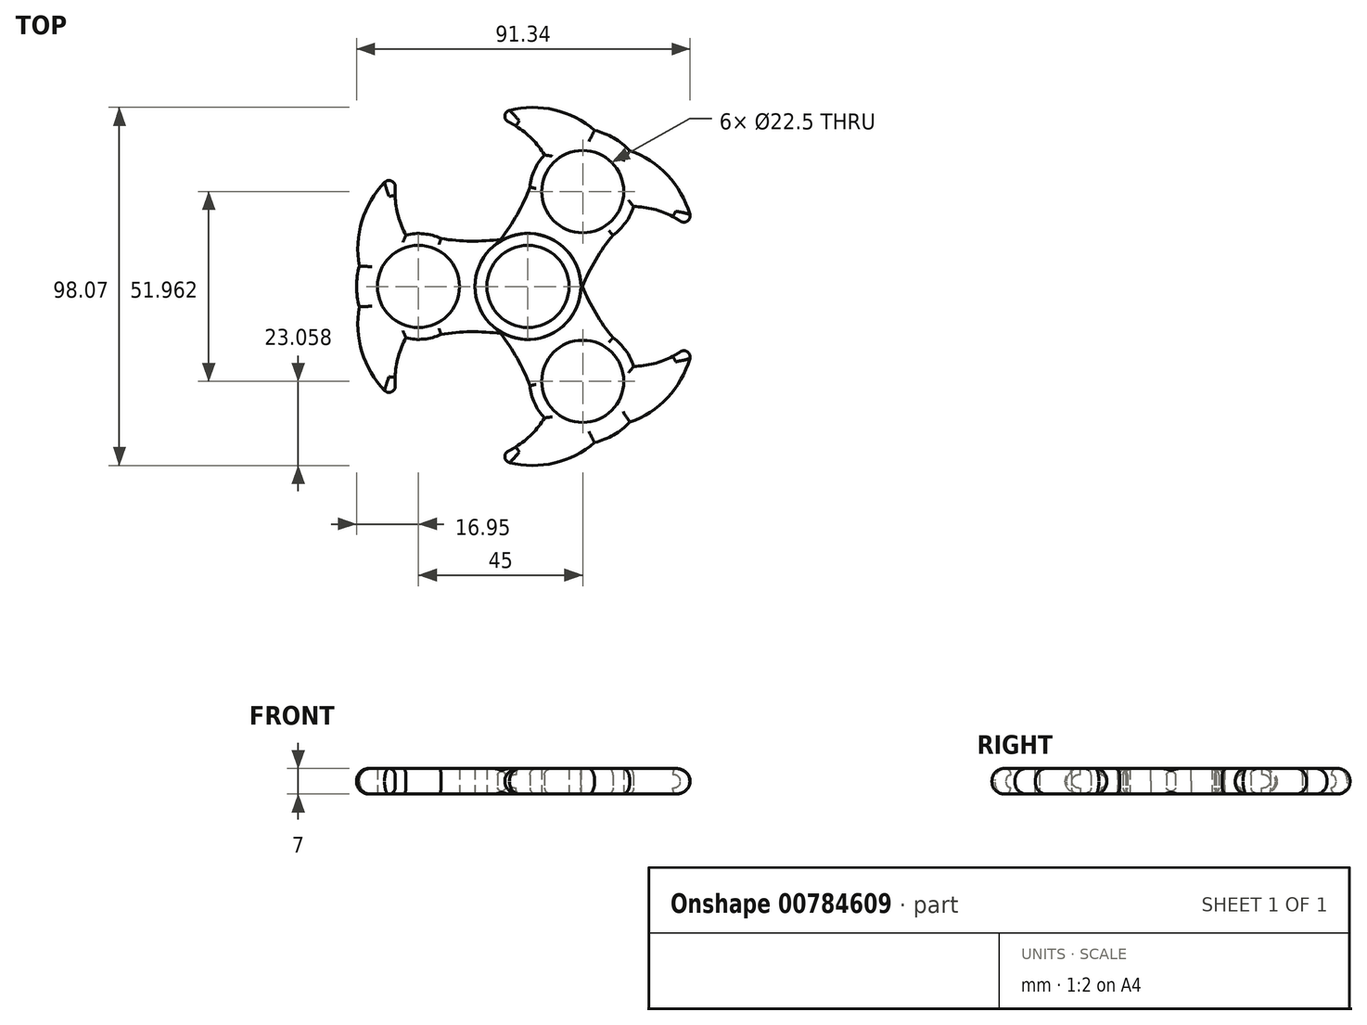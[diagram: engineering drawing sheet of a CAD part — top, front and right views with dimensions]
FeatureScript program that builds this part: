
annotation { "Feature Type Name" : "Feature", "Feature Type Description" : "" }
export const myFeature = defineFeature(function(context is Context, id is Id, definition is map)
    precondition{}
    {
        {
            var Q0;
            Q0=qCreatedBy(makeId("Top.planeOp"),FACE);
            var sketch = newSketch(context, id + "F0", { "sketchPlane" : qUnion([Q0])});
            skCircle(sketch, "E0", {"center": v(0, 0) * mm, "radius": 11.25 * mm});
            skLineSegment(sketch, "E1", {"start": v(0, 0) * mm, "end": v(-30, 0) * mm});
            skCircle(sketch, "E2", {"center": v(-30, 0) * mm, "radius": 11.25 * mm});
            skCircle(sketch, "E3", {"center": v(-30, 0) * mm, "radius": 14.5 * mm});
            skCircle(sketch, "E4", {"center": v(0, 0) * mm, "radius": 14.5 * mm});
            skArc(sketch, "E5", {"start": v(0, -14.5) * mm, "mid": v(-15, -12.4) * mm, "end": v(-30, -14.5) * mm});
            skArc(sketch, "E6.MirrorCS", {"start": v(0, 14.5) * mm, "mid": v(-15, 12.41) * mm, "end": v(-30, 14.5) * mm});
            skArc(sketch, "E7", {"start": v(-33.43, -14.08) * mm, "mid": v(-36.22, -22.63) * mm, "end": v(-35.67, -31.61) * mm});
            skArc(sketch, "E8", {"start": v(-44.5, 0) * mm, "mid": v(-45.64, -17.36) * mm, "end": v(-35.67, -31.61) * mm});
            skArc(sketch, "E9.MirrorCS", {"start": v(-33.43, 14.1) * mm, "mid": v(-36.22, 22.65) * mm, "end": v(-35.67, 31.63) * mm});
            skArc(sketch, "E10.MirrorCS", {"start": v(-44.5, 0.02) * mm, "mid": v(-45.64, 17.38) * mm, "end": v(-35.67, 31.63) * mm});
            skLineSegment(sketch, "E11", {"start": v(-44.5, 0.02) * mm, "end": v(-46.18, 0.02) * mm});
            skArc(sketch, "E12", {"start": v(-46.18, 5.59) * mm, "mid": v(-46.95, 0) * mm, "end": v(-46.18, -5.57) * mm});
            skSolve(sketch);
        }
        {
            var Q0;
            Q0 = qSketchRegion(id + "F0", true);
            extrude(context, id + "F1", {"entities" : qUnion([Q0]), "depth" : 7 * mm, "offsetDistance" : 25 * mm});
        }
        {
            var Q0;
            Q0=makeQuery(id+"F1.opExtrude","SWEPT_BODY",BODY,{"disambiguationData":[OSD([sQuery(id+"F0.wireOp",EDGE,"E0"),sQuery(id+"F0.wireOp",EDGE,"E2"),sQuery(id+"F0.wireOp",EDGE,"E3"),sQuery(id+"F0.wireOp",EDGE,"E4"),sQuery(id+"F0.wireOp",EDGE,"E5"),sQuery(id+"F0.wireOp",EDGE,"E6.MirrorCS"),sQuery(id+"F0.wireOp",EDGE,"N5z0aknD-i1vi-YF0C-1aPX-2y42hYEXv3Ia"),sQuery(id+"F0.wireOp",EDGE,"vDmnVq8P-OYbs-Mt9C-JsBL-gKGyEo7dJEWc")])]});
            var Q1;
            Q1=makeQuery(id+"F1.opExtrude","SWEPT_FACE",FACE,{"disambiguationData":[OSD([sQuery(id+"F0.wireOp",EDGE,"E4")])]});
            circularPattern(context, id + "F2", {"entities" : qUnion([Q0]), "axis" : qUnion([Q1]), "angle" : 360 * degree, "instanceCount" : 3, "equalSpace" : true});
        }
        {
            var Q0;
            Q0=makeQuery(id+"F2.opPattern","COPY",EDGE,{"derivedFrom":makeQuery(id+"F1.opExtrude","CAP_EDGE",EDGE,{"disambiguationData":[OSD([sQuery(id+"F0.wireOp",EDGE,"E10.MirrorCS")])],"isStart":false}),"instanceName":"2"});
            var Q1;
            Q1=makeQuery(id+"F2.opPattern","COPY",EDGE,{"derivedFrom":makeQuery(id+"F1.opExtrude","CAP_EDGE",EDGE,{"disambiguationData":[OSD([sQuery(id+"F0.wireOp",EDGE,"E12")])],"isStart":false}),"instanceName":"2"});
            var Q2;
            Q2=makeQuery(id+"F2.opPattern","COPY",EDGE,{"derivedFrom":makeQuery(id+"F1.opExtrude","CAP_EDGE",EDGE,{"disambiguationData":[OSD([sQuery(id+"F0.wireOp",EDGE,"E8")])],"isStart":false}),"instanceName":"2"});
            var Q3;
            Q3=makeQuery(id+"F2.opPattern","COPY",EDGE,{"derivedFrom":makeQuery(id+"F1.opExtrude","CAP_EDGE",EDGE,{"disambiguationData":[OSD([sQuery(id+"F0.wireOp",EDGE,"E10.MirrorCS")])],"isStart":false}),"instanceName":"1"});
            var Q4;
            Q4=makeQuery(id+"F2.opPattern","COPY",EDGE,{"derivedFrom":makeQuery(id+"F1.opExtrude","CAP_EDGE",EDGE,{"disambiguationData":[OSD([sQuery(id+"F0.wireOp",EDGE,"E12")])],"isStart":false}),"instanceName":"1"});
            var Q5;
            Q5=makeQuery(id+"F2.opPattern","COPY",EDGE,{"derivedFrom":makeQuery(id+"F1.opExtrude","CAP_EDGE",EDGE,{"disambiguationData":[OSD([sQuery(id+"F0.wireOp",EDGE,"E8")])],"isStart":false}),"instanceName":"1"});
            var Q6;
            Q6=makeQuery(id+"F1.opExtrude","CAP_EDGE",EDGE,{"disambiguationData":[OSD([sQuery(id+"F0.wireOp",EDGE,"E10.MirrorCS")])],"isStart":false});
            var Q7;
            Q7=makeQuery(id+"F1.opExtrude","CAP_EDGE",EDGE,{"disambiguationData":[OSD([sQuery(id+"F0.wireOp",EDGE,"E12")])],"isStart":false});
            var Q8;
            Q8=makeQuery(id+"F1.opExtrude","CAP_EDGE",EDGE,{"disambiguationData":[OSD([sQuery(id+"F0.wireOp",EDGE,"E8")])],"isStart":false});
            var Q9;
            Q9=makeQuery(id+"F1.opExtrude","CAP_EDGE",EDGE,{"disambiguationData":[OSD([sQuery(id+"F0.wireOp",EDGE,"E12")])],"isStart":true});
            var Q10;
            Q10=makeQuery(id+"F1.opExtrude","CAP_EDGE",EDGE,{"disambiguationData":[OSD([sQuery(id+"F0.wireOp",EDGE,"E8")])],"isStart":true});
            var Q11;
            Q11=makeQuery(id+"F1.opExtrude","CAP_EDGE",EDGE,{"disambiguationData":[OSD([sQuery(id+"F0.wireOp",EDGE,"E10.MirrorCS")])],"isStart":true});
            var Q12;
            Q12=makeQuery(id+"F2.opPattern","COPY",EDGE,{"derivedFrom":makeQuery(id+"F1.opExtrude","CAP_EDGE",EDGE,{"disambiguationData":[OSD([sQuery(id+"F0.wireOp",EDGE,"E12")])],"isStart":true}),"instanceName":"2"});
            var Q13;
            Q13=makeQuery(id+"F2.opPattern","COPY",EDGE,{"derivedFrom":makeQuery(id+"F1.opExtrude","CAP_EDGE",EDGE,{"disambiguationData":[OSD([sQuery(id+"F0.wireOp",EDGE,"E8")])],"isStart":true}),"instanceName":"2"});
            var Q14;
            Q14=makeQuery(id+"F2.opPattern","COPY",EDGE,{"derivedFrom":makeQuery(id+"F1.opExtrude","CAP_EDGE",EDGE,{"disambiguationData":[OSD([sQuery(id+"F0.wireOp",EDGE,"E10.MirrorCS")])],"isStart":true}),"instanceName":"2"});
            var Q15;
            Q15=makeQuery(id+"F2.opPattern","COPY",EDGE,{"derivedFrom":makeQuery(id+"F1.opExtrude","CAP_EDGE",EDGE,{"disambiguationData":[OSD([sQuery(id+"F0.wireOp",EDGE,"E10.MirrorCS")])],"isStart":true}),"instanceName":"1"});
            var Q16;
            Q16=makeQuery(id+"F2.opPattern","COPY",EDGE,{"derivedFrom":makeQuery(id+"F1.opExtrude","CAP_EDGE",EDGE,{"disambiguationData":[OSD([sQuery(id+"F0.wireOp",EDGE,"E12")])],"isStart":true}),"instanceName":"1"});
            var Q17;
            Q17=makeQuery(id+"F2.opPattern","COPY",EDGE,{"derivedFrom":makeQuery(id+"F1.opExtrude","CAP_EDGE",EDGE,{"disambiguationData":[OSD([sQuery(id+"F0.wireOp",EDGE,"E8")])],"isStart":true}),"instanceName":"1"});
            fillet(context, id + "F3", {"entities" : qUnion([Q0, Q1, Q2, Q3, Q4, Q5, Q6, Q7, Q8, Q9, Q10, Q11, Q12, Q13, Q14, Q15, Q16, Q17]), "radius" : 3.38 * mm, "tangentPropagation" : true, "allowEdgeOverflow" : false});
        }
        {
            var Q0;
            Q0=makeQuery(id+"F2.opPattern","COPY",EDGE,{"derivedFrom":makeQuery(id+"F1.opExtrude","CAP_EDGE",EDGE,{"disambiguationData":[OSD([sQuery(id+"F0.wireOp",EDGE,"E6.MirrorCS")])],"isStart":true}),"instanceName":"2"});
            var Q1;
            Q1=makeQuery(id+"F1.opExtrude","CAP_EDGE",EDGE,{"disambiguationData":[OSD([sQuery(id+"F0.wireOp",EDGE,"E5")])],"isStart":true});
            var Q2;
            Q2=makeQuery(id+"F2.opPattern","COPY",EDGE,{"derivedFrom":makeQuery(id+"F1.opExtrude","CAP_EDGE",EDGE,{"disambiguationData":[OSD([sQuery(id+"F0.wireOp",EDGE,"E5")])],"isStart":true}),"instanceName":"2"});
            var Q3;
            Q3=makeQuery(id+"F2.opPattern","COPY",EDGE,{"derivedFrom":makeQuery(id+"F1.opExtrude","CAP_EDGE",EDGE,{"disambiguationData":[OSD([sQuery(id+"F0.wireOp",EDGE,"E6.MirrorCS")])],"isStart":true}),"instanceName":"1"});
            var Q4;
            Q4=makeQuery(id+"F2.opPattern","COPY",EDGE,{"derivedFrom":makeQuery(id+"F1.opExtrude","CAP_EDGE",EDGE,{"disambiguationData":[OSD([sQuery(id+"F0.wireOp",EDGE,"E5")])],"isStart":true}),"instanceName":"1"});
            var Q5;
            Q5=makeQuery(id+"F1.opExtrude","CAP_EDGE",EDGE,{"disambiguationData":[OSD([sQuery(id+"F0.wireOp",EDGE,"E6.MirrorCS")])],"isStart":true});
            var Q6;
            {var subQ0=sQuery(id+"F0.wireOp",EDGE,"E6.MirrorCS");var subQ1=sQuery(id+"F0.wireOp",EDGE,"E3");var subQ2=makeQuery(id+"F0.imprint","INTERSECT",VERTEX,{"disambiguationData":[OD(0.0)],"derivedFrom":[subQ1,subQ0]});Q6=makeQuery(id+"F1.opExtrude","CAP_EDGE",EDGE,{"disambiguationData":[OSD([subQ1]),TDD([makeQuery(id+"F0.imprint","IMPRINT",EDGE,{"disambiguationData":[TD([[subQ2,1.0]])],"derivedFrom":subQ1}),makeQuery(id+"F0.imprint","IMPRINT",EDGE,{"disambiguationData":[TD([[subQ2,-1.0]])],"derivedFrom":subQ1})])],"isStart":true});}
            var Q7;
            {var subQ0=sQuery(id+"F0.wireOp",EDGE,"E5");var subQ1=sQuery(id+"F0.wireOp",EDGE,"E3");var subQ2=makeQuery(id+"F0.imprint","INTERSECT",VERTEX,{"disambiguationData":[OD(0.0)],"derivedFrom":[subQ1,subQ0]});Q7=makeQuery(id+"F2.opPattern","COPY",EDGE,{"derivedFrom":makeQuery(id+"F1.opExtrude","CAP_EDGE",EDGE,{"disambiguationData":[OSD([subQ1]),TDD([makeQuery(id+"F0.imprint","IMPRINT",EDGE,{"disambiguationData":[TD([[subQ2,1.0]])],"derivedFrom":subQ1}),makeQuery(id+"F0.imprint","IMPRINT",EDGE,{"disambiguationData":[TD([[subQ2,-1.0]])],"derivedFrom":subQ1})])],"isStart":true}),"instanceName":"1"});}
            var Q8;
            {var subQ0=sQuery(id+"F0.wireOp",EDGE,"E6.MirrorCS");var subQ1=sQuery(id+"F0.wireOp",EDGE,"E3");var subQ2=makeQuery(id+"F0.imprint","INTERSECT",VERTEX,{"disambiguationData":[OD(0.0)],"derivedFrom":[subQ1,subQ0]});Q8=makeQuery(id+"F2.opPattern","COPY",EDGE,{"derivedFrom":makeQuery(id+"F1.opExtrude","CAP_EDGE",EDGE,{"disambiguationData":[OSD([subQ1]),TDD([makeQuery(id+"F0.imprint","IMPRINT",EDGE,{"disambiguationData":[TD([[subQ2,1.0]])],"derivedFrom":subQ1}),makeQuery(id+"F0.imprint","IMPRINT",EDGE,{"disambiguationData":[TD([[subQ2,-1.0]])],"derivedFrom":subQ1})])],"isStart":true}),"instanceName":"1"});}
            var Q9;
            {var subQ0=sQuery(id+"F0.wireOp",EDGE,"E6.MirrorCS");var subQ1=sQuery(id+"F0.wireOp",EDGE,"E3");var subQ2=makeQuery(id+"F0.imprint","INTERSECT",VERTEX,{"disambiguationData":[OD(0.0)],"derivedFrom":[subQ1,subQ0]});Q9=makeQuery(id+"F2.opPattern","COPY",EDGE,{"derivedFrom":makeQuery(id+"F1.opExtrude","CAP_EDGE",EDGE,{"disambiguationData":[OSD([subQ1]),TDD([makeQuery(id+"F0.imprint","IMPRINT",EDGE,{"disambiguationData":[TD([[subQ2,1.0]])],"derivedFrom":subQ1}),makeQuery(id+"F0.imprint","IMPRINT",EDGE,{"disambiguationData":[TD([[subQ2,-1.0]])],"derivedFrom":subQ1})])],"isStart":true}),"instanceName":"2"});}
            var Q10;
            {var subQ0=sQuery(id+"F0.wireOp",EDGE,"E5");var subQ1=sQuery(id+"F0.wireOp",EDGE,"E3");var subQ2=makeQuery(id+"F0.imprint","INTERSECT",VERTEX,{"disambiguationData":[OD(0.0)],"derivedFrom":[subQ1,subQ0]});Q10=makeQuery(id+"F1.opExtrude","CAP_EDGE",EDGE,{"disambiguationData":[OSD([subQ1]),TDD([makeQuery(id+"F0.imprint","IMPRINT",EDGE,{"disambiguationData":[TD([[subQ2,1.0]])],"derivedFrom":subQ1}),makeQuery(id+"F0.imprint","IMPRINT",EDGE,{"disambiguationData":[TD([[subQ2,-1.0]])],"derivedFrom":subQ1})])],"isStart":true});}
            var Q11;
            {var subQ0=sQuery(id+"F0.wireOp",EDGE,"E5");var subQ1=sQuery(id+"F0.wireOp",EDGE,"E3");var subQ2=makeQuery(id+"F0.imprint","INTERSECT",VERTEX,{"disambiguationData":[OD(0.0)],"derivedFrom":[subQ1,subQ0]});Q11=makeQuery(id+"F2.opPattern","COPY",EDGE,{"derivedFrom":makeQuery(id+"F1.opExtrude","CAP_EDGE",EDGE,{"disambiguationData":[OSD([subQ1]),TDD([makeQuery(id+"F0.imprint","IMPRINT",EDGE,{"disambiguationData":[TD([[subQ2,1.0]])],"derivedFrom":subQ1}),makeQuery(id+"F0.imprint","IMPRINT",EDGE,{"disambiguationData":[TD([[subQ2,-1.0]])],"derivedFrom":subQ1})])],"isStart":true}),"instanceName":"2"});}
            var Q12;
            {var subQ0=sQuery(id+"F0.wireOp",EDGE,"E6.MirrorCS");var subQ1=sQuery(id+"F0.wireOp",EDGE,"E3");var subQ2=makeQuery(id+"F0.imprint","INTERSECT",VERTEX,{"disambiguationData":[OD(0.0)],"derivedFrom":[subQ1,subQ0]});Q12=makeQuery(id+"F2.opPattern","COPY",EDGE,{"derivedFrom":makeQuery(id+"F1.opExtrude","CAP_EDGE",EDGE,{"disambiguationData":[OSD([subQ1]),TDD([makeQuery(id+"F0.imprint","IMPRINT",EDGE,{"disambiguationData":[TD([[subQ2,1.0]])],"derivedFrom":subQ1}),makeQuery(id+"F0.imprint","IMPRINT",EDGE,{"disambiguationData":[TD([[subQ2,-1.0]])],"derivedFrom":subQ1})])],"isStart":false}),"instanceName":"2"});}
            var Q13;
            Q13=makeQuery(id+"F2.opPattern","COPY",EDGE,{"derivedFrom":makeQuery(id+"F1.opExtrude","CAP_EDGE",EDGE,{"disambiguationData":[OSD([sQuery(id+"F0.wireOp",EDGE,"E6.MirrorCS")])],"isStart":false}),"instanceName":"2"});
            var Q14;
            Q14=makeQuery(id+"F1.opExtrude","CAP_EDGE",EDGE,{"disambiguationData":[OSD([sQuery(id+"F0.wireOp",EDGE,"E5")])],"isStart":false});
            var Q15;
            {var subQ0=sQuery(id+"F0.wireOp",EDGE,"E5");var subQ1=sQuery(id+"F0.wireOp",EDGE,"E3");var subQ2=makeQuery(id+"F0.imprint","INTERSECT",VERTEX,{"disambiguationData":[OD(0.0)],"derivedFrom":[subQ1,subQ0]});Q15=makeQuery(id+"F1.opExtrude","CAP_EDGE",EDGE,{"disambiguationData":[OSD([subQ1]),TDD([makeQuery(id+"F0.imprint","IMPRINT",EDGE,{"disambiguationData":[TD([[subQ2,1.0]])],"derivedFrom":subQ1}),makeQuery(id+"F0.imprint","IMPRINT",EDGE,{"disambiguationData":[TD([[subQ2,-1.0]])],"derivedFrom":subQ1})])],"isStart":false});}
            var Q16;
            Q16=makeQuery(id+"F1.opExtrude","CAP_EDGE",EDGE,{"disambiguationData":[OSD([sQuery(id+"F0.wireOp",EDGE,"E6.MirrorCS")])],"isStart":false});
            var Q17;
            {var subQ0=sQuery(id+"F0.wireOp",EDGE,"E6.MirrorCS");var subQ1=sQuery(id+"F0.wireOp",EDGE,"E3");var subQ2=makeQuery(id+"F0.imprint","INTERSECT",VERTEX,{"disambiguationData":[OD(0.0)],"derivedFrom":[subQ1,subQ0]});Q17=makeQuery(id+"F1.opExtrude","CAP_EDGE",EDGE,{"disambiguationData":[OSD([subQ1]),TDD([makeQuery(id+"F0.imprint","IMPRINT",EDGE,{"disambiguationData":[TD([[subQ2,1.0]])],"derivedFrom":subQ1}),makeQuery(id+"F0.imprint","IMPRINT",EDGE,{"disambiguationData":[TD([[subQ2,-1.0]])],"derivedFrom":subQ1})])],"isStart":false});}
            var Q18;
            Q18=makeQuery(id+"F2.opPattern","COPY",EDGE,{"derivedFrom":makeQuery(id+"F1.opExtrude","CAP_EDGE",EDGE,{"disambiguationData":[OSD([sQuery(id+"F0.wireOp",EDGE,"E5")])],"isStart":false}),"instanceName":"1"});
            var Q19;
            {var subQ0=sQuery(id+"F0.wireOp",EDGE,"E5");var subQ1=sQuery(id+"F0.wireOp",EDGE,"E3");var subQ2=makeQuery(id+"F0.imprint","INTERSECT",VERTEX,{"disambiguationData":[OD(0.0)],"derivedFrom":[subQ1,subQ0]});Q19=makeQuery(id+"F2.opPattern","COPY",EDGE,{"derivedFrom":makeQuery(id+"F1.opExtrude","CAP_EDGE",EDGE,{"disambiguationData":[OSD([subQ1]),TDD([makeQuery(id+"F0.imprint","IMPRINT",EDGE,{"disambiguationData":[TD([[subQ2,1.0]])],"derivedFrom":subQ1}),makeQuery(id+"F0.imprint","IMPRINT",EDGE,{"disambiguationData":[TD([[subQ2,-1.0]])],"derivedFrom":subQ1})])],"isStart":false}),"instanceName":"1"});}
            var Q20;
            Q20=makeQuery(id+"F2.opPattern","COPY",EDGE,{"derivedFrom":makeQuery(id+"F1.opExtrude","CAP_EDGE",EDGE,{"disambiguationData":[OSD([sQuery(id+"F0.wireOp",EDGE,"E6.MirrorCS")])],"isStart":false}),"instanceName":"1"});
            var Q21;
            Q21=makeQuery(id+"F2.opPattern","COPY",EDGE,{"derivedFrom":makeQuery(id+"F1.opExtrude","CAP_EDGE",EDGE,{"disambiguationData":[OSD([sQuery(id+"F0.wireOp",EDGE,"E5")])],"isStart":false}),"instanceName":"2"});
            var Q22;
            {var subQ0=sQuery(id+"F0.wireOp",EDGE,"E5");var subQ1=sQuery(id+"F0.wireOp",EDGE,"E3");var subQ2=makeQuery(id+"F0.imprint","INTERSECT",VERTEX,{"disambiguationData":[OD(0.0)],"derivedFrom":[subQ1,subQ0]});Q22=makeQuery(id+"F2.opPattern","COPY",EDGE,{"derivedFrom":makeQuery(id+"F1.opExtrude","CAP_EDGE",EDGE,{"disambiguationData":[OSD([subQ1]),TDD([makeQuery(id+"F0.imprint","IMPRINT",EDGE,{"disambiguationData":[TD([[subQ2,1.0]])],"derivedFrom":subQ1}),makeQuery(id+"F0.imprint","IMPRINT",EDGE,{"disambiguationData":[TD([[subQ2,-1.0]])],"derivedFrom":subQ1})])],"isStart":false}),"instanceName":"2"});}
            var Q23;
            {var subQ0=sQuery(id+"F0.wireOp",EDGE,"E6.MirrorCS");var subQ1=sQuery(id+"F0.wireOp",EDGE,"E3");var subQ2=makeQuery(id+"F0.imprint","INTERSECT",VERTEX,{"disambiguationData":[OD(0.0)],"derivedFrom":[subQ1,subQ0]});Q23=makeQuery(id+"F2.opPattern","COPY",EDGE,{"derivedFrom":makeQuery(id+"F1.opExtrude","CAP_EDGE",EDGE,{"disambiguationData":[OSD([subQ1]),TDD([makeQuery(id+"F0.imprint","IMPRINT",EDGE,{"disambiguationData":[TD([[subQ2,1.0]])],"derivedFrom":subQ1}),makeQuery(id+"F0.imprint","IMPRINT",EDGE,{"disambiguationData":[TD([[subQ2,-1.0]])],"derivedFrom":subQ1})])],"isStart":false}),"instanceName":"1"});}
            var Q24;
            Q24=makeQuery(id+"F2.opPattern","COPY",EDGE,{"derivedFrom":makeQuery(id+"F1.opExtrude","CAP_EDGE",EDGE,{"disambiguationData":[OSD([sQuery(id+"F0.wireOp",EDGE,"E9.MirrorCS")])],"isStart":false}),"instanceName":"2"});
            var Q25;
            Q25=makeQuery(id+"F2.opPattern","COPY",EDGE,{"derivedFrom":makeQuery(id+"F1.opExtrude","CAP_EDGE",EDGE,{"disambiguationData":[OSD([sQuery(id+"F0.wireOp",EDGE,"E9.MirrorCS")])],"isStart":true}),"instanceName":"2"});
            var Q26;
            Q26=makeQuery(id+"F1.opExtrude","CAP_EDGE",EDGE,{"disambiguationData":[OSD([sQuery(id+"F0.wireOp",EDGE,"E7")])],"isStart":false});
            var Q27;
            Q27=makeQuery(id+"F1.opExtrude","CAP_EDGE",EDGE,{"disambiguationData":[OSD([sQuery(id+"F0.wireOp",EDGE,"E7")])],"isStart":true});
            var Q28;
            Q28=makeQuery(id+"F1.opExtrude","CAP_EDGE",EDGE,{"disambiguationData":[OSD([sQuery(id+"F0.wireOp",EDGE,"E9.MirrorCS")])],"isStart":false});
            var Q29;
            Q29=makeQuery(id+"F2.opPattern","COPY",EDGE,{"derivedFrom":makeQuery(id+"F1.opExtrude","CAP_EDGE",EDGE,{"disambiguationData":[OSD([sQuery(id+"F0.wireOp",EDGE,"E9.MirrorCS")])],"isStart":false}),"instanceName":"1"});
            var Q30;
            Q30=makeQuery(id+"F2.opPattern","COPY",EDGE,{"derivedFrom":makeQuery(id+"F1.opExtrude","CAP_EDGE",EDGE,{"disambiguationData":[OSD([sQuery(id+"F0.wireOp",EDGE,"E7")])],"isStart":false}),"instanceName":"2"});
            var Q31;
            Q31=makeQuery(id+"F2.opPattern","COPY",EDGE,{"derivedFrom":makeQuery(id+"F1.opExtrude","CAP_EDGE",EDGE,{"disambiguationData":[OSD([sQuery(id+"F0.wireOp",EDGE,"E7")])],"isStart":true}),"instanceName":"1"});
            fillet(context, id + "F4", {"entities" : qUnion([Q0, Q1, Q2, Q3, Q4, Q5, Q6, Q7, Q8, Q9, Q10, Q11, Q12, Q13, Q14, Q15, Q16, Q17, Q18, Q19, Q20, Q21, Q22, Q23, Q24, Q25, Q26, Q27, Q28, Q29, Q30, Q31]), "radius" : 1.69 * mm, "tangentPropagation" : true, "allowEdgeOverflow" : false});
        }
    });
